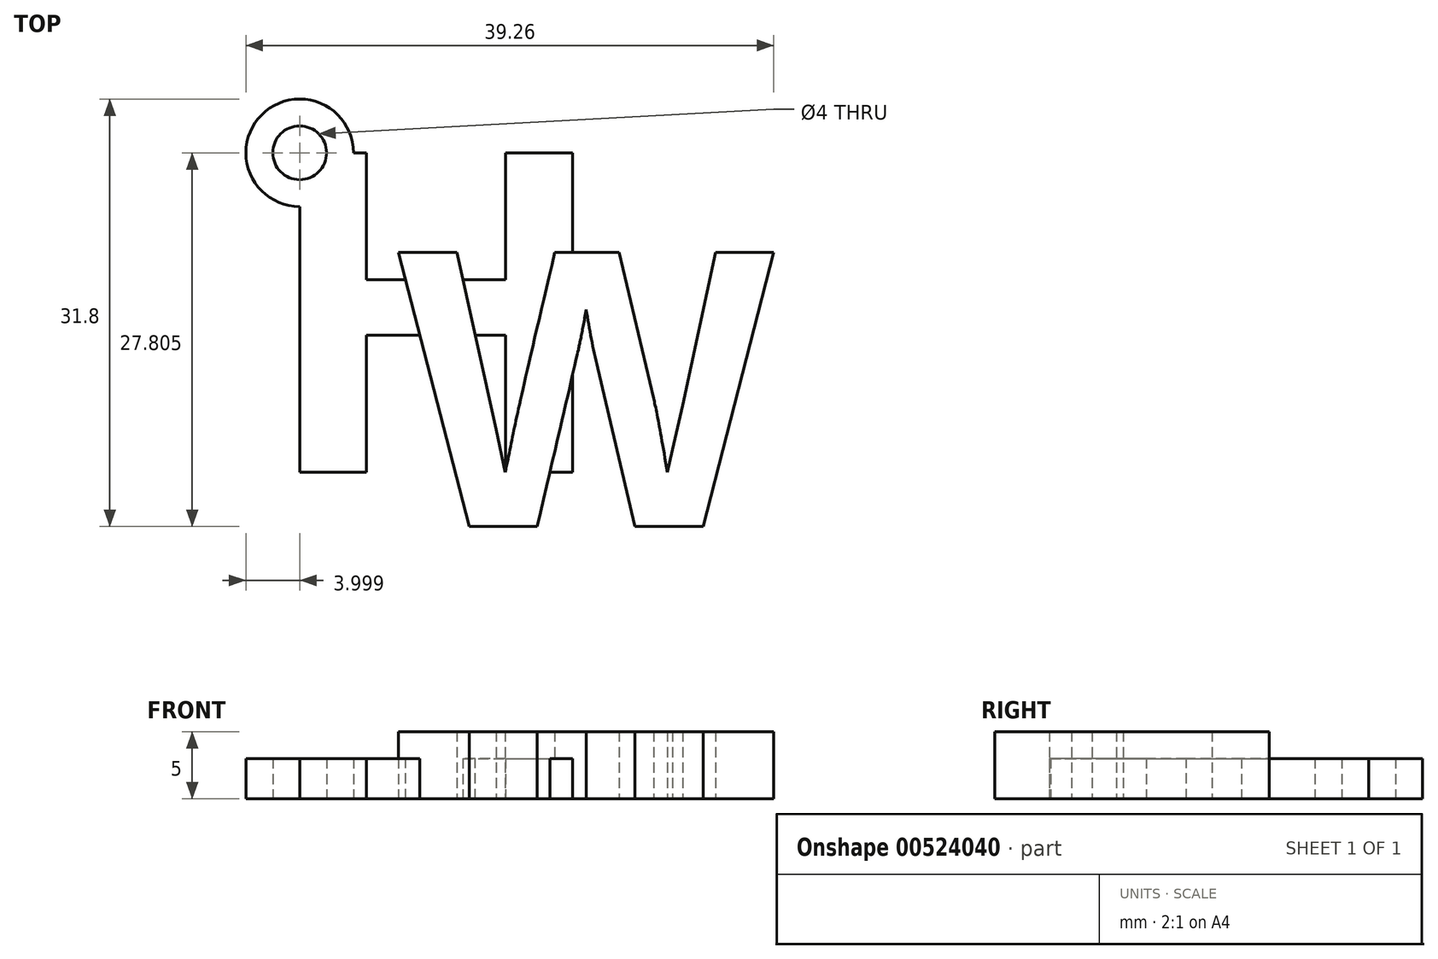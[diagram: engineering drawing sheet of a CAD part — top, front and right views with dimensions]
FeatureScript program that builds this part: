
annotation { "Feature Type Name" : "Feature", "Feature Type Description" : "" }
export const myFeature = defineFeature(function(context is Context, id is Id, definition is map)
    precondition{}
    {
        {
            var Q0;
            Q0=qCreatedBy(makeId("Top.planeOp"),FACE);
            var sketch = newSketch(context, id + "F0", { "sketchPlane" : qUnion([Q0])});
            skText(sketch, "E0", { "text": "H", "fontName": "Arimo-Bold.ttf"});
            const initialGuessF0  = {"E0": [-0.06195, 0.00948, 1, 0, 0.02485]};
            skSetInitialGuess(sketch, initialGuessF0);
            skSolve(sketch);
        }
        {
            var Q0;
            Q0 = qSketchRegion(id + "F0", true);
            extrude(context, id + "F1", {"entities" : qUnion([Q0]), "depth" : 3 * mm, "offsetDistance" : 25 * mm});
        }
        {
            var Q0;
            Q0=qCreatedBy(makeId("Top.planeOp"),FACE);
            var sketch = newSketch(context, id + "F2", { "sketchPlane" : qUnion([Q0])});
            skText(sketch, "E1", { "text": "W", "fontName": "Arimo-Bold.ttf"});
            const initialGuessF2  = {"E1": [-0.05232, 0.00542, 1, 0, 0.02134]};
            skSetInitialGuess(sketch, initialGuessF2);
            skSolve(sketch);
        }
        {
            var Q0;
            Q0=makeQuery(id+"F2.imprint","IMPRINT",FACE,{"disambiguationData":[TD([[makeQuery(id+"F2.imprint","IMPRINT",EDGE,{"derivedFrom":sQuery(id+"F2.wireOp",EDGE,"E1.sketch_text.stroke-0")}),-1.0]])]});
            extrude(context, id + "F3", {"entities" : qUnion([Q0]), "operationType" : NewBodyOperationType.ADD, "depth" : 5 * mm, "offsetDistance" : 25 * mm});
        }
        {
            var Q0;
            Q0=qCreatedBy(makeId("Top.planeOp"),FACE);
            var sketch = newSketch(context, id + "F4", { "sketchPlane" : qUnion([Q0])});
            skLineSegment(sketch, "E2.0.0", {"start": v(-37.04, 19.66) * mm, "end": v(-36.44, 17.13) * mm});
            skLineSegment(sketch, "E2.0.1", {"start": v(-36.44, 17.13) * mm, "end": v(-36.44, 33.22) * mm});
            skLineSegment(sketch, "E2.0.2", {"start": v(-36.44, 33.22) * mm, "end": v(-44.32, 33.22) * mm});
            skLineSegment(sketch, "E2.0.3", {"start": v(-44.32, 33.22) * mm, "end": v(-44.32, 23.77) * mm});
            skLineSegment(sketch, "E2.0.4", {"start": v(-44.32, 23.77) * mm, "end": v(-54.67, 23.77) * mm});
            skLineSegment(sketch, "E2.0.5", {"start": v(-54.67, 23.77) * mm, "end": v(-54.67, 33.22) * mm});
            skLineSegment(sketch, "E2.0.6", {"start": v(-54.67, 33.22) * mm, "end": v(-59.64, 33.22) * mm});
            skLineSegment(sketch, "E2.0.7", {"start": v(-59.64, 33.22) * mm, "end": v(-59.64, 9.48) * mm});
            skLineSegment(sketch, "E2.0.8", {"start": v(-59.64, 9.48) * mm, "end": v(-54.67, 9.48) * mm});
            skLineSegment(sketch, "E2.0.9", {"start": v(-54.67, 9.48) * mm, "end": v(-54.67, 19.66) * mm});
            skLineSegment(sketch, "E2.0.10", {"start": v(-54.67, 19.66) * mm, "end": v(-50.7, 19.66) * mm});
            skLineSegment(sketch, "E2.0.11", {"start": v(-50.7, 19.66) * mm, "end": v(-50.7, 19.66) * mm});
            skLineSegment(sketch, "E2.0.12", {"start": v(-50.7, 19.66) * mm, "end": v(-47.1, 19.66) * mm});
            skLineSegment(sketch, "E2.0.13", {"start": v(-47.1, 19.66) * mm, "end": v(-46.7, 17.92) * mm});
            skLineSegment(sketch, "E2.0.14", {"start": v(-46.7, 17.92) * mm, "end": v(-41.43, 17.92) * mm});
            skFitSpline(sketch, "E2.0.15", {"points": [v(-41.02, 19.66) * mm, v(-43.1, 10.76) * mm, v(-43.43, 9.23) * mm]});
            skLineSegment(sketch, "E2.0.16", {"start": v(-41.02, 19.66) * mm, "end": v(-37.04, 19.66) * mm});
            skCircle(sketch, "E3", {"center": v(-59.64, 33.22) * mm, "radius": 2 * mm});
            skCircle(sketch, "E4", {"center": v(-59.64, 33.22) * mm, "radius": 4 * mm});
            skSolve(sketch);
        }
        {
            var Q0;
            {var subQ0=sQuery(id+"F4.wireOp",EDGE,"E2.0.7");var subQ1=sQuery(id+"F4.wireOp",EDGE,"E2.0.6");var subQ2=makeQuery(id+"F4.imprint","INTERSECT",VERTEX,{"derivedFrom":[subQ1,subQ0]});Q0=makeQuery(id+"F4.imprint","IMPRINT",FACE,{"disambiguationData":[TD([[makeQuery(id+"F4.imprint","IMPRINT",EDGE,{"disambiguationData":[TD([[subQ2,1.0]])],"derivedFrom":subQ1}),1.0]])]});}
            extrude(context, id + "F5", {"entities" : qUnion([Q0]), "operationType" : NewBodyOperationType.REMOVE, "depth" : 4 * mm, "offsetDistance" : 25 * mm});
        }
        {
            var Q0;
            {var subQ0=sQuery(id+"F4.wireOp",EDGE,"E4");var subQ1=sQuery(id+"F4.wireOp",EDGE,"E2.0.6");var subQ2=makeQuery(id+"F4.imprint","INTERSECT",VERTEX,{"derivedFrom":[subQ1,subQ0]});Q0=makeQuery(id+"F4.imprint","IMPRINT",FACE,{"disambiguationData":[TD([[makeQuery(id+"F4.imprint","IMPRINT",EDGE,{"disambiguationData":[TD([[subQ2,-1.0]])],"derivedFrom":subQ1}),-1.0]])]});}
            extrude(context, id + "F6", {"entities" : qUnion([Q0]), "operationType" : NewBodyOperationType.ADD, "depth" : 3 * mm, "offsetDistance" : 25 * mm});
        }
    });
